# Revit family: ePump
name_source: partatom
category: Mechanical Equipment
units: mm (PartAtom-declared; Revit-internal decimal feet)

## family parameters
Always vertical = Yes
Classification = Pump
Cut with Voids When Loaded = No
OmniClass Number = 23.60.30.21
OmniClass Title = Pumps
Part Type = Normal
Room Calculation Point = No
Round Connector Dimension = Use Radius
Shared = No
Work Plane-Based = No

## types (4) — shared parameters
Anchor Points (Center to Center) = 9"
Assembly Code = D2090400
Black = Fluidra Base
Description = Jandy Variable Speed ePump Dual Voltage 2 Aux Relays
Fluidra_Amps_(115V) = 16 A
Fluidra_Amps_(230V) = 11 A
Fluidra_Apparent_Load = 0 VA
Fluidra_Cos ϕ = 100.00%
Fluidra_Description = Jandy Variable Speed ePump Dual Voltage 2 Aux Relays
Fluidra_Frequency = 60 Hz
Fluidra_Manufacturer = Fluidra
Fluidra_Phase = 1
Fluidra_Recommended_Pipe_Size = 2" -3"
Fluidra_Union_Size = 2" - 2.5"
Fluidra_Voltage (High) = 230 V
Fluidra_Voltage (Low) = 115 V
Fluidra_Weight = 71.00 lb
Front to Anchor Points (Center) = 11 5/8"
Front to Outlet (Center) = 14"
Inlet Height (Center) = 10 3/8"
Lid = Fluidra Lid
Manufacturer = Fluidra
Pump Height = 15 1/4"
Pump Length = 30 1/8"
Pump Width (Lid Tabs) = 12 15/16"
URL = https://www.jandy.com
Union Diameter = 2"

## per-type parameters (varying)
| type | Fluidra_Horsepower | Fluidra_Max_Watts_(115V) | Fluidra_Max_Watts_(230V) | Fluidra_WEF_(115V) | Fluidra_WEF_(230V) | SpeedSet Controller |
| VSSHP220DV2A | 2 hp | 1660 W | 2190 W | 8.8 | 8.5 | No |
| VSSHP220DV2AS | 2 hp | 1660 W | 2190 W | 8.8 | 8.5 | Yes |
| VSSHP270DV2A | 3 hp | 1675 W | 2370 W | 9.3 | 7.5 | No |
| VSSHP270DV2AS | 3 hp | 1675 W | 2370 W | 9.3 | 7.5 | Yes |

note: column(s) folded — value = type name in every type: Fluidra_Model, Model

## geometry (parser evidence)
native form markers: Sweep x10
no freeform markers — native parametric forms only
